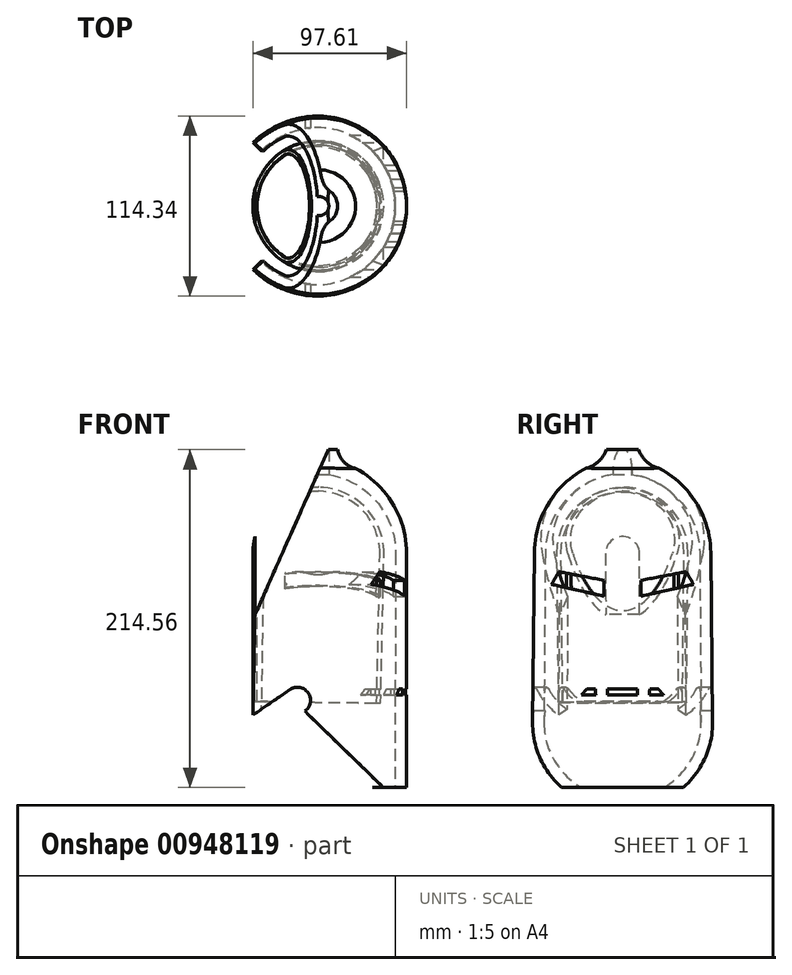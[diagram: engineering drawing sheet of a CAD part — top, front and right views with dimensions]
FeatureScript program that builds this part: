
annotation { "Feature Type Name" : "Feature", "Feature Type Description" : "" }
export const myFeature = defineFeature(function(context is Context, id is Id, definition is map)
    precondition{}
    {
        {
            var Q0;
            Q0=qCreatedBy(makeId("Front.planeOp"),FACE);
            var sketch = newSketch(context, id + "F0", { "sketchPlane" : qUnion([Q0])});
            skLineSegment(sketch, "E0", {"start": v(-40.59, 38.9) * mm, "end": v(-40.59, -55.2) * mm});
            skLineSegment(sketch, "E1", {"start": v(43.51, 38.9) * mm, "end": v(43.51, -55.2) * mm, "construction": true});
            skArc(sketch, "E2", {"start": v(50.07, 38.9) * mm, "mid": v(38.08, 71.7) * mm, "end": v(7.66, 88.88) * mm});
            skLineSegment(sketch, "E3", {"start": v(7.66, 88.88) * mm, "end": v(7.66, 104.76) * mm});
            skLineSegment(sketch, "E4", {"start": v(7.66, 104.76) * mm, "end": v(13.23, 104.76) * mm});
            skArc(sketch, "E5", {"start": v(57.02, 38.9) * mm, "mid": v(48.3, 70.37) * mm, "end": v(24.6, 92.87) * mm});
            skArc(sketch, "E6", {"start": v(13.23, 104.76) * mm, "mid": v(17.1, 97.07) * mm, "end": v(24.6, 92.87) * mm});
            skLineSegment(sketch, "E7", {"start": v(50.07, 38.9) * mm, "end": v(49.64, -109.73) * mm});
            skLineSegment(sketch, "E8", {"start": v(49.64, -109.73) * mm, "end": v(57.02, -109.73) * mm});
            skLineSegment(sketch, "E9", {"start": v(57.02, -109.73) * mm, "end": v(57.02, 38.9) * mm});
            skLineSegment(sketch, "E10", {"start": v(1.46, 80.94) * mm, "end": v(0, -55.2) * mm});
            skArc(sketch, "E11", {"start": v(1.46, 80.94) * mm, "mid": v(-28.27, 68.63) * mm, "end": v(-40.59, 38.9) * mm});
            skArc(sketch, "E12", {"start": v(43.51, 38.9) * mm, "mid": v(31.2, 68.63) * mm, "end": v(1.46, 80.94) * mm, "construction": true});
            skLineSegment(sketch, "E13", {"start": v(-40.59, -55.2) * mm, "end": v(0, -55.2) * mm});
            skLineSegment(sketch, "E14", {"start": v(0, -55.2) * mm, "end": v(43.51, -55.2) * mm, "construction": true});
            skSolve(sketch);
        }
        {
            var Q0;
            {var subQ3=sQuery(id+"F0.wireOp",EDGE,"E10");Q0=makeQuery(id+"F0.imprint","IMPRINT",FACE,{"disambiguationData":[TD([[makeQuery(id+"F0.imprint","IMPRINT",EDGE,{"derivedFrom":subQ3}),-1.0]])]});}
            var Q1;
            Q1=sQuery(id+"F0.wireOp",EDGE,"E10");
            revolve(context, id + "F1", {"surfaceOperationType" : NewSurfaceOperationType.NEW, "entities" : qUnion([Q0]), "axis" : qUnion([Q1]), "revolveType" : RevolveType.FULL});
        }
        {
            var Q0;
            Q0=makeQuery(id+"F1.opRevolve","SWEPT_FACE",FACE,{"disambiguationData":[OSD([sQuery(id+"F0.wireOp",EDGE,"E13")])]});
            shell(context, id + "F2", {"entities" : qUnion([Q0]), "thickness" : 2.54 * mm});
        }
        {
            var Q0;
            Q0=makeQuery(id+"F0.imprint","IMPRINT",FACE,{"disambiguationData":[TD([[makeQuery(id+"F0.imprint","IMPRINT",EDGE,{"derivedFrom":sQuery(id+"F0.wireOp",EDGE,"E2")}),-1.0]])]});
            var Q1;
            Q1=sQuery(id+"F0.wireOp",EDGE,"E10");
            revolve(context, id + "F3", {"surfaceOperationType" : NewSurfaceOperationType.NEW, "entities" : qUnion([Q0]), "axis" : qUnion([Q1]), "revolveType" : RevolveType.SYMMETRIC, "angle" : 270 * degree});
        }
        {
            var Q0;
            Q0=qCreatedBy(makeId("Front.planeOp"),FACE);
            cPlane(context, id + "F4", {"entities" : qUnion([Q0]), "cplaneType" : CPlaneType.OFFSET, "offset" : 79.25 * mm, "width" : 152.4 * mm, "height" : 152.4 * mm});
        }
        {
            var Q0;
            Q0=qCreatedBy(id+"F4.planeOp",FACE);
            var sketch = newSketch(context, id + "F5", { "sketchPlane" : qUnion([Q0])});
            skLineSegment(sketch, "E15", {"start": v(7.36, 104.98) * mm, "end": v(-35.9, 104.98) * mm});
            skLineSegment(sketch, "E16", {"start": v(-35.9, 104.98) * mm, "end": v(-39.18, 104.98) * mm});
            skLineSegment(sketch, "E17", {"start": v(-39.18, 104.98) * mm, "end": v(-39.18, 0) * mm});
            skLineSegment(sketch, "E18", {"start": v(-39.18, 0) * mm, "end": v(7.36, 104.98) * mm});
            skLineSegment(sketch, "E19", {"start": v(-40.6, -63.84) * mm, "end": v(-17.08, -47.57) * mm});
            skArc(sketch, "E20", {"start": v(-7.6, -61.27) * mm, "mid": v(-5.5, -49.69) * mm, "end": v(-17.08, -47.57) * mm});
            skLineSegment(sketch, "E21", {"start": v(-40.6, -63.84) * mm, "end": v(-46.49, -67.47) * mm});
            skLineSegment(sketch, "E22", {"start": v(-46.49, -67.47) * mm, "end": v(-46.49, -109.58) * mm});
            skLineSegment(sketch, "E23", {"start": v(-46.49, -109.58) * mm, "end": v(42.03, -109.58) * mm});
            skLineSegment(sketch, "E24", {"start": v(42.03, -109.58) * mm, "end": v(-7.6, -61.27) * mm});
            skSolve(sketch);
        }
        {
            var Q0;
            Q0=makeQuery(id+"F5.imprint","IMPRINT",FACE,{"disambiguationData":[TD([[makeQuery(id+"F5.imprint","IMPRINT",EDGE,{"derivedFrom":sQuery(id+"F5.wireOp",EDGE,"E15")}),1.0]])]});
            extrude(context, id + "F6", {"entities" : qUnion([Q0]), "operationType" : NewBodyOperationType.REMOVE, "oppositeDirection" : true, "depth" : 141.48 * mm, "offsetDistance" : 25.4 * mm});
        }
        {
            var Q0;
            Q0=makeQuery(id+"F5.imprint","IMPRINT",FACE,{"disambiguationData":[TD([[makeQuery(id+"F5.imprint","IMPRINT",EDGE,{"derivedFrom":sQuery(id+"F5.wireOp",EDGE,"TkEp7Cqa-ZAUk-QqQ3-qQ3a-RaLuY6nay3tP")}),1.0]])]});
            var Q1;
            Q1=makeQuery(id+"F5.imprint","IMPRINT",FACE,{"disambiguationData":[TD([[makeQuery(id+"F5.imprint","IMPRINT",EDGE,{"derivedFrom":sQuery(id+"F5.wireOp",EDGE,"E19")}),-1.0]])]});
            extrude(context, id + "F7", {"entities" : qUnion([Q0, Q1]), "operationType" : NewBodyOperationType.REMOVE, "endBound" : BoundingType.THROUGH_ALL, "oppositeDirection" : true, "depth" : 25.4 * mm, "offsetDistance" : 25.4 * mm});
        }
        {
            var Q0;
            Q0=qCreatedBy(makeId("Right.planeOp"),FACE);
            cPlane(context, id + "F8", {"entities" : qUnion([Q0]), "cplaneType" : CPlaneType.OFFSET, "offset" : 93.22 * mm, "width" : 152.4 * mm, "height" : 152.4 * mm});
        }
        {
            var Q0;
            Q0=qCreatedBy(id+"F8.planeOp",FACE);
            var sketch = newSketch(context, id + "F9", { "sketchPlane" : qUnion([Q0])});
            skLineSegment(sketch, "E25", {"start": v(-40.42, 27.28) * mm, "end": v(-45.07, 19.26) * mm});
            skLineSegment(sketch, "E26", {"start": v(-45.07, 19.26) * mm, "end": v(-11.72, 11.66) * mm});
            skLineSegment(sketch, "E27", {"start": v(-11.72, 11.66) * mm, "end": v(-11.72, 21.8) * mm});
            skLineSegment(sketch, "E28.MirrorCS", {"start": v(11.72, 11.66) * mm, "end": v(11.72, 21.8) * mm});
            skLineSegment(sketch, "E29.MirrorCS", {"start": v(45.07, 19.26) * mm, "end": v(11.72, 11.66) * mm});
            skLineSegment(sketch, "E30.MirrorCS", {"start": v(40.42, 27.28) * mm, "end": v(45.07, 19.26) * mm});
            skLineSegment(sketch, "E31", {"start": v(-40.42, 27.28) * mm, "end": v(-11.72, 21.8) * mm});
            skLineSegment(sketch, "E32", {"start": v(11.72, 21.8) * mm, "end": v(40.42, 27.28) * mm});
            skSolve(sketch);
        }
        {
            var Q0;
            Q0=makeQuery(id+"F9.imprint","IMPRINT",FACE,{"disambiguationData":[TD([[makeQuery(id+"F9.imprint","IMPRINT",EDGE,{"derivedFrom":sQuery(id+"F9.wireOp",EDGE,"E28.MirrorCS")}),-1.0]])]});
            var Q1;
            Q1=makeQuery(id+"F9.imprint","IMPRINT",FACE,{"disambiguationData":[TD([[makeQuery(id+"F9.imprint","IMPRINT",EDGE,{"derivedFrom":sQuery(id+"F9.wireOp",EDGE,"E25")}),1.0]])]});
            extrude(context, id + "F10", {"entities" : qUnion([Q0, Q1]), "operationType" : NewBodyOperationType.REMOVE, "oppositeDirection" : true, "depth" : 113.54 * mm, "offsetDistance" : 25.4 * mm});
        }
        {
            var Q0;
            Q0=qCreatedBy(id+"F8.planeOp",FACE);
            var sketch = newSketch(context, id + "F11", { "sketchPlane" : qUnion([Q0])});
            skLineSegment(sketch, "E33", {"start": v(-17.33, -47.11) * mm, "end": v(-22.6, -47.11) * mm});
            skLineSegment(sketch, "E34", {"start": v(-22.6, -47.11) * mm, "end": v(-26, -50.83) * mm});
            skLineSegment(sketch, "E35", {"start": v(-26, -50.83) * mm, "end": v(-17.02, -50.83) * mm});
            skLineSegment(sketch, "E36", {"start": v(-17.02, -50.83) * mm, "end": v(-17.33, -47.11) * mm});
            skLineSegment(sketch, "E37", {"start": v(-9.59, -47.11) * mm, "end": v(-9.59, -50.83) * mm});
            skLineSegment(sketch, "E38", {"start": v(-9.59, -50.83) * mm, "end": v(0, -50.83) * mm});
            skLineSegment(sketch, "E39", {"start": v(0, -47.11) * mm, "end": v(-9.59, -47.11) * mm});
            skLineSegment(sketch, "E40", {"start": v(0, -47.11) * mm, "end": v(0, -50.83) * mm});
            skLineSegment(sketch, "E41.MirrorCS", {"start": v(0, -47.11) * mm, "end": v(9.59, -47.11) * mm});
            skLineSegment(sketch, "E42.MirrorCS", {"start": v(9.59, -47.11) * mm, "end": v(9.59, -50.83) * mm});
            skLineSegment(sketch, "E43.MirrorCS", {"start": v(9.59, -50.83) * mm, "end": v(0, -50.83) * mm});
            skLineSegment(sketch, "E44.MirrorCS", {"start": v(17.02, -50.83) * mm, "end": v(17.33, -47.11) * mm});
            skLineSegment(sketch, "E45.MirrorCS", {"start": v(17.33, -47.11) * mm, "end": v(22.6, -47.11) * mm});
            skLineSegment(sketch, "E46.MirrorCS", {"start": v(22.6, -47.11) * mm, "end": v(26, -50.83) * mm});
            skLineSegment(sketch, "E47.MirrorCS", {"start": v(26, -50.83) * mm, "end": v(17.02, -50.83) * mm});
            skPoint(sketch, "E48.orphan", {"position": v(12.06, -47.11) * mm});
            skPoint(sketch, "E49.orphan", {"position": v(-12.06, -47.11) * mm});
            skSolve(sketch);
        }
        {
            var Q0;
            Q0=makeQuery(id+"F11.imprint","IMPRINT",FACE,{"disambiguationData":[TD([[makeQuery(id+"F11.imprint","IMPRINT",EDGE,{"derivedFrom":sQuery(id+"F11.wireOp",EDGE,"E33")}),1.0]])]});
            var Q1;
            Q1=makeQuery(id+"F11.imprint","IMPRINT",FACE,{"disambiguationData":[TD([[makeQuery(id+"F11.imprint","IMPRINT",EDGE,{"derivedFrom":sQuery(id+"F11.wireOp",EDGE,"E40")}),1.0]])]});
            var Q2;
            Q2=makeQuery(id+"F11.imprint","IMPRINT",FACE,{"disambiguationData":[TD([[makeQuery(id+"F11.imprint","IMPRINT",EDGE,{"derivedFrom":sQuery(id+"F11.wireOp",EDGE,"E37")}),1.0]])]});
            var Q3;
            Q3=makeQuery(id+"F11.imprint","IMPRINT",FACE,{"disambiguationData":[TD([[makeQuery(id+"F11.imprint","IMPRINT",EDGE,{"derivedFrom":sQuery(id+"F11.wireOp",EDGE,"E44.MirrorCS")}),-1.0]])]});
            extrude(context, id + "F12", {"entities" : qUnion([Q0, Q1, Q2, Q3]), "operationType" : NewBodyOperationType.REMOVE, "oppositeDirection" : true, "depth" : 82.3 * mm, "offsetDistance" : 25.4 * mm});
        }
    });
